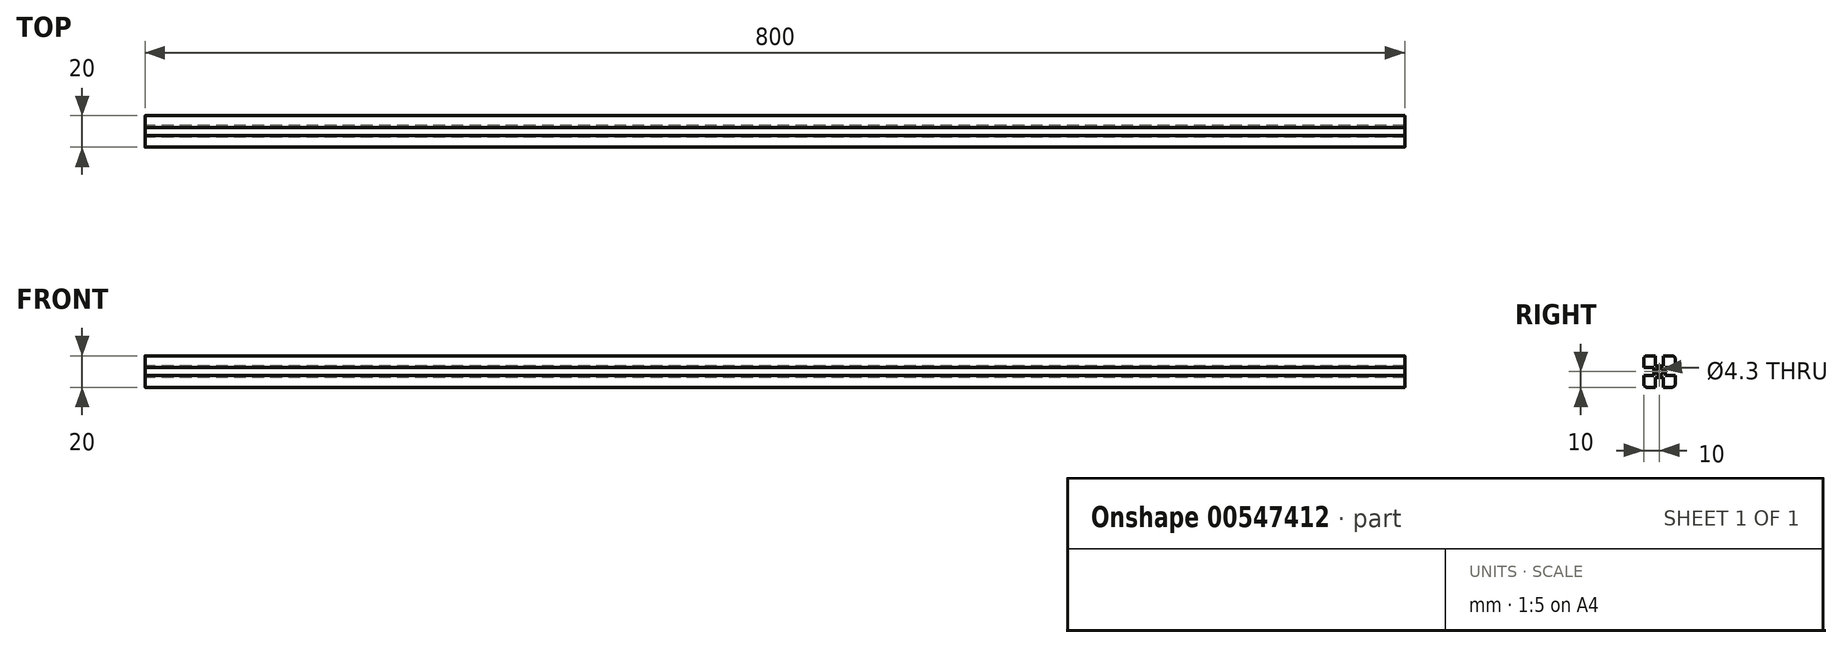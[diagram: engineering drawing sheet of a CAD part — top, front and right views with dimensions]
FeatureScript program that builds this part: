
annotation { "Feature Type Name" : "Feature", "Feature Type Description" : "" }
export const myFeature = defineFeature(function(context is Context, id is Id, definition is map)
    precondition{}
    {
        {
            var Q0;
            Q0=qCreatedBy(makeId("Right.planeOp"),FACE);
            var sketch = newSketch(context, id + "F0", { "sketchPlane" : qUnion([Q0])});
            skLineSegment(sketch, "E0.bottom", {"start": v(-10, 10) * mm, "end": v(-2.5, 10) * mm});
            skLineSegment(sketch, "E0.top", {"start": v(-10, -10) * mm, "end": v(-2.5, -10) * mm});
            skLineSegment(sketch, "E0.left", {"start": v(-10, 10) * mm, "end": v(-10, 2.5) * mm});
            skLineSegment(sketch, "E0.right", {"start": v(10, 10) * mm, "end": v(10, 2.5) * mm});
            skPoint(sketch, "E0.middle", {"position": v(0, 0) * mm});
            skLineSegment(sketch, "E1.top", {"start": v(2.5, 3.65) * mm, "end": v(-2.5, 3.65) * mm});
            skLineSegment(sketch, "E1.left", {"start": v(2.5, 10) * mm, "end": v(2.5, 3.65) * mm});
            skLineSegment(sketch, "E1.right", {"start": v(-2.5, 10) * mm, "end": v(-2.5, 3.65) * mm});
            skLineSegment(sketch, "E2.bottom", {"start": v(10, 2.5) * mm, "end": v(3.65, 2.5) * mm});
            skLineSegment(sketch, "E2.top", {"start": v(10, -2.5) * mm, "end": v(3.65, -2.5) * mm});
            skLineSegment(sketch, "E2.right", {"start": v(3.65, 2.5) * mm, "end": v(3.65, -2.5) * mm});
            skLineSegment(sketch, "E3.top", {"start": v(2.5, -3.65) * mm, "end": v(-2.5, -3.65) * mm});
            skLineSegment(sketch, "E3.left", {"start": v(2.5, -10) * mm, "end": v(2.5, -3.65) * mm});
            skLineSegment(sketch, "E3.right", {"start": v(-2.5, -10) * mm, "end": v(-2.5, -3.65) * mm});
            skLineSegment(sketch, "E4.bottom", {"start": v(-10, 2.5) * mm, "end": v(-3.65, 2.5) * mm});
            skLineSegment(sketch, "E4.top", {"start": v(-10, -2.5) * mm, "end": v(-3.65, -2.5) * mm});
            skLineSegment(sketch, "E4.right", {"start": v(-3.65, 2.5) * mm, "end": v(-3.65, -2.5) * mm});
            skLineSegment(sketch, "E5.trimOffspring", {"start": v(-10, -2.5) * mm, "end": v(-10, -10) * mm});
            skLineSegment(sketch, "E6.trimOffspring", {"start": v(2.5, 10) * mm, "end": v(10, 10) * mm});
            skLineSegment(sketch, "E7.trimOffspring", {"start": v(10, -2.5) * mm, "end": v(10, -10) * mm});
            skLineSegment(sketch, "E8.trimOffspring", {"start": v(2.5, -10) * mm, "end": v(10, -10) * mm});
            skSolve(sketch);
        }
        {
            var Q0;
            Q0 = qSketchRegion(id + "F0", true);
            extrude(context, id + "F1", {"entities" : qUnion([Q0]), "endBound" : BoundingType.SYMMETRIC, "depth" : 800 * mm, "offsetDistance" : 25 * mm});
        }
        {
            var Q0;
            Q0=makeQuery(id+"F1.opExtrude","CAP_FACE",FACE,{"disambiguationData":[OSD([sQuery(id+"F0.wireOp",EDGE,"E0.bottom"),sQuery(id+"F0.wireOp",EDGE,"E0.top"),sQuery(id+"F0.wireOp",EDGE,"E0.left"),sQuery(id+"F0.wireOp",EDGE,"E0.right"),sQuery(id+"F0.wireOp",EDGE,"E1.top"),sQuery(id+"F0.wireOp",EDGE,"E1.left"),sQuery(id+"F0.wireOp",EDGE,"E1.right"),sQuery(id+"F0.wireOp",EDGE,"E2.bottom"),sQuery(id+"F0.wireOp",EDGE,"E2.top"),sQuery(id+"F0.wireOp",EDGE,"E2.right"),sQuery(id+"F0.wireOp",EDGE,"E3.top"),sQuery(id+"F0.wireOp",EDGE,"E3.left"),sQuery(id+"F0.wireOp",EDGE,"E3.right"),sQuery(id+"F0.wireOp",EDGE,"E4.bottom"),sQuery(id+"F0.wireOp",EDGE,"E4.top"),sQuery(id+"F0.wireOp",EDGE,"E4.right"),sQuery(id+"F0.wireOp",EDGE,"E5.trimOffspring"),sQuery(id+"F0.wireOp",EDGE,"E6.trimOffspring"),sQuery(id+"F0.wireOp",EDGE,"E7.trimOffspring"),sQuery(id+"F0.wireOp",EDGE,"E8.trimOffspring")])],"isStart":true});
            var sketch = newSketch(context, id + "F2", { "sketchPlane" : qUnion([Q0])});
            skCircle(sketch, "E9", {"center": v(0, 0) * mm, "radius": 2.15 * mm});
            skSolve(sketch);
        }
        {
            var Q0;
            Q0 = qSketchRegion(id + "F2", true);
            extrude(context, id + "F3", {"entities" : qUnion([Q0]), "operationType" : NewBodyOperationType.REMOVE, "oppositeDirection" : true, "depth" : 800 * mm, "offsetDistance" : 25 * mm});
        }
        {
            var Q0;
            Q0=makeQuery(id+"F1.opExtrude","SWEPT_EDGE",EDGE,{"disambiguationData":[OSD([sQuery(id+"F0.wireOp",EDGE,"E7.trimOffspring"),sQuery(id+"F0.wireOp",EDGE,"E8.trimOffspring")])]});
            var Q1;
            Q1=makeQuery(id+"F1.opExtrude","SWEPT_EDGE",EDGE,{"disambiguationData":[OSD([sQuery(id+"F0.wireOp",EDGE,"E0.top"),sQuery(id+"F0.wireOp",EDGE,"E5.trimOffspring")])]});
            var Q2;
            Q2=makeQuery(id+"F1.opExtrude","SWEPT_EDGE",EDGE,{"disambiguationData":[OSD([sQuery(id+"F0.wireOp",EDGE,"E0.bottom"),sQuery(id+"F0.wireOp",EDGE,"E0.left")])]});
            var Q3;
            Q3=makeQuery(id+"F1.opExtrude","SWEPT_EDGE",EDGE,{"disambiguationData":[OSD([sQuery(id+"F0.wireOp",EDGE,"E0.right"),sQuery(id+"F0.wireOp",EDGE,"E6.trimOffspring")])]});
            fillet(context, id + "F4", {"entities" : qUnion([Q0, Q1, Q2, Q3]), "radius" : 2 * mm, "tangentPropagation" : true, "allowEdgeOverflow" : false});
        }
    });
